# Revit family: ASH_Contour21_Multiproduct_BIM_GB_S6456;S6457;S6458;S6459;S6460;S6461;S6462
name_source: partatom
category: Plumbing Fixtures
revit_build: Autodesk Revit MEP 2014 (Build: 20130308_1515(x64)
units: mm (PartAtom-declared; Revit-internal decimal feet)

## types (35) — shared parameters
AccessibilityPerformance = Doc M
Accessories = www.idealspec.co.uk
AreaUnits = millimeters
Assembly Code = C1030200
AssetType = Fixed
BREEAMApproved = No
Brand = Armitage Shanks
ConnectionType = Plumbing
DurationUnit = year
ECA = No
ExpectedLife = 30
Help = www.idealspec.co.uk/contact-us.html
IfcExportAs = IfcValveType
IfcExportType = FAUCET
InstallationInstructions = www.idealspec.co.uk/resources.html
LinearUnits = millimeters
ManufacturerURL = www.idealspec.co.uk
Material = Brass
NBSDescription = Support rails
NBSReference = 45-35-70/360
NettWeight = 0.62 Kg
NominalHeight = 35 mm  [stored 0.114829 ft]
NominalWidth = 100 mm  [stored 0.328084 ft]
Shape = Sculptured
Space = Internal
SpareParts = www.fastpart-spares.co.uk
TMV3 = Yes
URL = www.idealspec.co.uk
Uniclass2015Description = Support Rails
Uniclass2015Reference = Pr_40_20_76_84
Uniclass2015Version = Products v1.1
Version = 1
VolumeUnits = Litres
WRAS = Yes
WarrantyDescription = Manufacturers Warranty
WarrantyDurationParts = 5
WarrantyDurationUnit = year
WaterEfficientProduct = No
zero-valued in all types: CWFU, Cost, Default Elevation, HWFU, WFU

## per-type parameters (varying)
| type | BIMObjectName | BarCode | Color | Description | Features | Finish | FinishMtl | Model | ModelNumber | ModelReference | Name | NominalLength | ProductInformation | Size |
| S645736 - Contour21 800 x 350mm - Blue | ASH_ArmitageShanks_GrabRails_Contour21_S645736 | 5017830384915 | Blue | Contour21 800 x 350mm, blue | 800 x 350mm, blue | Blue | ASH_ArmitageShanks_Brassware_Blue_36_Render | S645736 | S645736 | Contour21 800 x 350mm, blue | GrabRails_Contour21_S645736_ArmitageShanks | 800 mm  [stored 2.62467 ft] | www.idealspec.co.uk/assets/datasheet/S645736 | 35 x 800 x 100 mm |
| S645839 - Contour21 900 x 350mm - Blue | ASH_ArmitageShanks_GrabRails_Contour21_S645839 | 0 | Blue | Contour21 900 x 350mm, blue | 900 x 350mm, blue | Blue | ASH_ArmitageShanks_Brassware_Blue_36_Render | S645839 | S645839 | Contour21 900 x 350mm, blue | GrabRails_Contour21_S645839_ArmitageShanks | 900 mm  [stored 2.95276 ft] | www.idealspec.co.uk/assets/datasheet/S645839 | 35 x 900 x 100 mm |
| S645936 - Contour21 1000 x 350mm - Blue | ASH_ArmitageShanks_GrabRails_Contour21_S645936 | 5017830384939 | Blue | Contour21 1000 x 350mm, blue | 1000 x 350mm, blue | Blue | ASH_ArmitageShanks_Brassware_Blue_36_Render | S645936 | S645936 | Contour21 1000 x 350mm, blue | GrabRails_Contour21_S645936_ArmitageShanks | 1000 mm  [stored 3.28084 ft] | www.idealspec.co.uk/assets/datasheet/S645936 | 35 x 1000 x 100 mm |
| S646036 - Contour21 1100 x 350mm - Blue | ASH_ArmitageShanks_GrabRails_Contour21_S646036 | 5017830384946 | Blue | Contour21 1100 x 350mm, blue | 1100 x 350mm, blue | Blue | ASH_ArmitageShanks_Brassware_Blue_36_Render | S646036 | S646036 | Contour21 1100 x 350mm, blue | GrabRails_Contour21_S646036_ArmitageShanks | 1100 mm | www.idealspec.co.uk/assets/datasheet/S646036 | 35 x 1100 x 100 mm |
| S646136 - Contour21 1200 x 350mm - Blue | ASH_ArmitageShanks_GrabRails_Contour21_S646136 | 5017830384953 | Blue | Contour21 1200 x 350mm, blue | 1200 x 350mm, blue | Blue | ASH_ArmitageShanks_Brassware_Blue_36_Render | S646136 | S646136 | Contour21 1200 x 350mm, blue | GrabRails_Contour21_S646136_ArmitageShanks | 1200 mm | www.idealspec.co.uk/assets/datasheet/S646136 | 35 x 1200 x 100 mm |
| S646236 - Contour21 1750 x 350mm - Blue | ASH_ArmitageShanks_GrabRails_Contour21_S646236 | 5017830384960 | Blue | Contour21 1750 x 350mm, blue | 1750 x 350mm, blue | Blue | ASH_ArmitageShanks_Brassware_Blue_36_Render | S646236 | S646236 | Contour21 1750 x 350mm, blue | GrabRails_Contour21_S646236_ArmitageShanks | 1750 mm  [stored 5.74147 ft] | www.idealspec.co.uk/assets/datasheet/S646236 | 35 x 1750 x 100 mm |
| S6457AC - Contour21 800 x 350mm - White | ASH_ArmitageShanks_GrabRails_Contour21_S6457AC | 5017830383796 | White | Contour21 800 x 350mm, white | 800 x 350mm, white | White | ASH_ArmitageShanks_Brassware_White_AC_Render | S6457AC | S6457AC | Contour21 800 x 350mm, white | GrabRails_Contour21_S6457AC_ArmitageShanks | 800 mm  [stored 2.62467 ft] | www.idealspec.co.uk/assets/datasheet/S6457AC | 35 x 800 x 100 mm |
| S6457LJ - Contour21 800 x 350mm - Grey | ASH_ArmitageShanks_GrabRails_Contour21_S6457LJ | 5017830384595 | Grey | Contour21 800 x 350mm, grey | 800 x 350mm, grey | Grey | ASH_ArmitageShanks_Brassware_Grey_LJ_Render | S6457LJ | S6457LJ | Contour21 800 x 350mm, grey | GrabRails_Contour21_S6457LJ_ArmitageShanks | 800 mm  [stored 2.62467 ft] | www.idealspec.co.uk/assets/datasheet/S6457LJ | 35 x 800 x 100 mm |
| S6457MY - Contour21 800 x 350mm - Stainless Steel | ASH_ArmitageShanks_GrabRails_Contour21_S6457MY | 5017830384274 | Steel | Contour21 800 x 350mm, stainless steel | 800 x 350mm, stainless steel | Steel | ASH_ArmitageShanks_Brassware_Steel_MY_Render | S6457MY | S6457MY | Contour21 800 x 350mm, stainless steel | GrabRails_Contour21_S6457MY_ArmitageShanks | 800 mm  [stored 2.62467 ft] | www.idealspec.co.uk/assets/datasheet/S6457MY | 35 x 800 x 100 mm |
| S6457RN - Contour21 800 x 350mm - Charcoal | ASH_ArmitageShanks_GrabRails_Contour21_S6457RN | 0 | Charcoal | Contour21 800 x 350mm, charcoal | 800 x 350mm, charcoal | Charcoal | ASH_ArmitageShanks_Brassware_Charcoal_RN_Render | S6457RN | S6457RN | Contour21 800 x 350mm, charcoal | GrabRails_Contour21_S6457RN_ArmitageShanks | 800 mm  [stored 2.62467 ft] | www.idealspec.co.uk/assets/datasheet/S6457RN | 35 x 800 x 100 mm |
| S6459AC - Contour21 1000 x 350mm - White | ASH_ArmitageShanks_GrabRails_Contour21_S6459AC | 5017830383819 | White | Contour21 1000 x 350mm, white | 1000 x 350mm, white | White | ASH_ArmitageShanks_Brassware_White_AC_Render | S6459AC | S6459AC | Contour21 1000 x 350mm, white | GrabRails_Contour21_S6459AC_ArmitageShanks | 1000 mm  [stored 3.28084 ft] | www.idealspec.co.uk/assets/datasheet/S6459AC | 35 x 1000 x 100 mm |
| S6459LJ - Contour21 1000 x 350mm - Grey | ASH_ArmitageShanks_GrabRails_Contour21_S6459LJ | 5017830384618 | Grey | Contour21 1000 x 350mm, grey | 1000 x 350mm, grey | Grey | ASH_ArmitageShanks_Brassware_Grey_LJ_Render | S6459LJ | S6459LJ | Contour21 1000 x 350mm, grey | GrabRails_Contour21_S6459LJ_ArmitageShanks | 1000 mm  [stored 3.28084 ft] | www.idealspec.co.uk/assets/datasheet/S6459LJ | 35 x 1000 x 100 mm |
| S6459MY - Contour21 1000 x 350mm - Stainless Steel | ASH_ArmitageShanks_GrabRails_Contour21_S6459MY | 5017830384298 | Steel | Contour21 1000 x 350mm, stainless steel | 1000 x 350mm, stainless steel | Steel | ASH_ArmitageShanks_Brassware_Steel_MY_Render | S6459MY | S6459MY | Contour21 1000 x 350mm, stainless steel | GrabRails_Contour21_S6459MY_ArmitageShanks | 1000 mm  [stored 3.28084 ft] | www.idealspec.co.uk/assets/datasheet/S6459MY | 35 x 1000 x 100 mm |
| S6459RN - Contour21 1000 x 350mm - Charcoal | ASH_ArmitageShanks_GrabRails_Contour21_S6459RN | 5017830388470 | Charcoal | Contour21 1000 x 350mm, charcoal | 1000 x 350mm, charcoal | Charcoal | ASH_ArmitageShanks_Brassware_Charcoal_RN_Render | S6459RN | S6459RN | Contour21 1000 x 350mm, charcoal | GrabRails_Contour21_S6459RN_ArmitageShanks | 1000 mm  [stored 3.28084 ft] | www.idealspec.co.uk/assets/datasheet/S6459RN | 35 x 1000 x 100 mm |
| S6460AC - Contour21 1100 x 350mm - White | ASH_ArmitageShanks_GrabRails_Contour21_S6460AC | 5017830383826 | White | Contour21 1100 x 350mm, white | 1100 x 350mm, white | White | ASH_ArmitageShanks_Brassware_White_AC_Render | S6460AC | S6460AC | Contour21 1100 x 350mm, white | GrabRails_Contour21_S6460AC_ArmitageShanks | 1100 mm | www.idealspec.co.uk/assets/datasheet/S6460AC | 35 x 1100 x 100 mm |
| S6460LJ - Contour21 1100 x 350mm - Grey | ASH_ArmitageShanks_GrabRails_Contour21_S6460LJ | 5017830384625 | Grey | Contour21 1100 x 350mm, grey | 1100 x 350mm, grey | Grey | ASH_ArmitageShanks_Brassware_Grey_LJ_Render | S6460LJ | S6460LJ | Contour21 1100 x 350mm, grey | GrabRails_Contour21_S6460LJ_ArmitageShanks | 1100 mm | www.idealspec.co.uk/assets/datasheet/S6460LJ | 35 x 1100 x 100 mm |
| S6460MY - Contour21 1100 x 350mm - Stainless Steel | ASH_ArmitageShanks_GrabRails_Contour21_S6460MY | 5017830384304 | Steel | Contour21 1100 x 350mm, stainless steel | 1100 x 350mm, stainless steel | Steel | ASH_ArmitageShanks_Brassware_Steel_MY_Render | S6460MY | S6460MY | Contour21 1100 x 350mm, stainless steel | GrabRails_Contour21_S6460MY_ArmitageShanks | 1100 mm | www.idealspec.co.uk/assets/datasheet/S6460MY | 35 x 1100 x 100 mm |
| S6460RN - Contour21 1100 x 350mm - Charcoal | ASH_ArmitageShanks_GrabRails_Contour21_S6460RN | 5017830388487 | Charcoal | Contour21 1100 x 350mm, charcoal | 1100 x 350mm, charcoal | Charcoal | ASH_ArmitageShanks_Brassware_Charcoal_RN_Render | S6460RN | S6460RN | Contour21 1100 x 350mm, charcoal | GrabRails_Contour21_S6460RN_ArmitageShanks | 1100 mm | www.idealspec.co.uk/assets/datasheet/S6460RN | 35 x 1100 x 100 mm |
| S6461AC - Contour21 1200 x 350mm - White | ASH_ArmitageShanks_GrabRails_Contour21_S6461AC | 5017830383833 | White | Contour21 1200 x 350mm, white | 1200 x 350mm, white | White | ASH_ArmitageShanks_Brassware_White_AC_Render | S6461AC | S6461AC | Contour21 1200 x 350mm, white | GrabRails_Contour21_S6461AC_ArmitageShanks | 1200 mm | www.idealspec.co.uk/assets/datasheet/S6461AC | 35 x 1200 x 100 mm |
| S6461LJ - Contour21 1200 x 350mm - Grey | ASH_ArmitageShanks_GrabRails_Contour21_S6461LJ | 5017830384632 | Grey | Contour21 1200 x 350mm, grey | 1200 x 350mm, grey | Grey | ASH_ArmitageShanks_Brassware_Grey_LJ_Render | S6461LJ | S6461LJ | Contour21 1200 x 350mm, grey | GrabRails_Contour21_S6461LJ_ArmitageShanks | 1200 mm | www.idealspec.co.uk/assets/datasheet/S6461LJ | 35 x 1200 x 100 mm |
| S6461MY - Contour21 1200 x 350mm - Stainless Steel | ASH_ArmitageShanks_GrabRails_Contour21_S6461MY | 5017830384311 | Steel | Contour21 1200 x 350mm, stainless steel | 1200 x 350mm, stainless steel | Steel | ASH_ArmitageShanks_Brassware_Steel_MY_Render | S6461MY | S6461MY | Contour21 1200 x 350mm, stainless steel | GrabRails_Contour21_S6461MY_ArmitageShanks | 1200 mm | www.idealspec.co.uk/assets/datasheet/S6461MY | 35 x 1200 x 100 mm |
| S6461RN - Contour21 1200 x 350mm - Charcoal | ASH_ArmitageShanks_GrabRails_Contour21_S6461RN | 5017830388494 | Charcoal | Contour21 1200 x 350mm, charcoal | 1200 x 350mm, charcoal | Charcoal | ASH_ArmitageShanks_Brassware_Charcoal_RN_Render | S6461RN | S6461RN | Contour21 1200 x 350mm, charcoal | GrabRails_Contour21_S6461RN_ArmitageShanks | 1200 mm | www.idealspec.co.uk/assets/datasheet/S6461RN | 35 x 1200 x 100 mm |
| S6458AC - Contour21 900 x 350mm - White | ASH_ArmitageShanks_GrabRails_Contour21_S6458AC | 5017830383802 | White | Contour21 900 x 350mm, white | 900 x 350mm, white | White | ASH_ArmitageShanks_Brassware_White_AC_Render | S6458AC | S6458AC | Contour21 900 x 350mm, white | GrabRails_Contour21_S6458AC_ArmitageShanks | 900 mm  [stored 2.95276 ft] | www.idealspec.co.uk/assets/datasheet/S6458AC | 35 x 900 x 100 mm |
| S6458LJ - Contour21 900 x 350mm - Grey | ASH_ArmitageShanks_GrabRails_Contour21_S6458LJ | 5017830384601 | Grey | Contour21 900 x 350mm, grey | 900 x 350mm, grey | Grey | ASH_ArmitageShanks_Brassware_Grey_LJ_Render | S6458LJ | S6458LJ | Contour21 900 x 350mm, grey | GrabRails_Contour21_S6458LJ_ArmitageShanks | 900 mm  [stored 2.95276 ft] | www.idealspec.co.uk/assets/datasheet/S6458LJ | 35 x 900 x 100 mm |
| S6458MY - Contour21 900 x 350mm - Stainless Steel | ASH_ArmitageShanks_GrabRails_Contour21_S6458MY | 5017830384281 | Steel | Contour21 900 x 350mm, stainless steel | 900 x 350mm, stainless steel | Steel | ASH_ArmitageShanks_Brassware_Steel_MY_Render | S6458MY | S6458MY | Contour21 900 x 350mm, stainless steel | GrabRails_Contour21_S6458MY_ArmitageShanks | 900 mm  [stored 2.95276 ft] | www.idealspec.co.uk/assets/datasheet/S6458MY | 35 x 900 x 100 mm |
| S6458RN - Contour21 900 x 350mm - Charcoal | ASH_ArmitageShanks_GrabRails_Contour21_S6458RN | 5017830388463 | Charcoal | Contour21 900 x 350mm, charcoal | 900 x 350mm, charcoal | Charcoal | ASH_ArmitageShanks_Brassware_Charcoal_RN_Render | S6458RN | S6458RN | Contour21 900 x 350mm, charcoal | GrabRails_Contour21_S6458RN_ArmitageShanks | 900 mm  [stored 2.95276 ft] | www.idealspec.co.uk/assets/datasheet/S6458RN | 35 x 900 x 100 mm |
| S6462AC - Contour21 1750 x 350mm - White | ASH_ArmitageShanks_GrabRails_Contour21_S6462AC | 5017830383840 | White | Contour21 1750 x 350mm, white | 1750 x 350mm, white | White | ASH_ArmitageShanks_Brassware_White_AC_Render | S6462AC | S6462AC | Contour21 1750 x 350mm, white | GrabRails_Contour21_S6462AC_ArmitageShanks | 1750 mm  [stored 5.74147 ft] | www.idealspec.co.uk/assets/datasheet/S6462AC | 35 x 1750 x 100 mm |
| S6462LJ - Contour21 1750 x 350mm - Grey | ASH_ArmitageShanks_GrabRails_Contour21_S6462LJ | 5017830384649 | Grey | Contour21 1750 x 350mm, grey | 1750 x 350mm, grey | Grey | ASH_ArmitageShanks_Brassware_Grey_LJ_Render | S6462LJ | S6462LJ | Contour21 1750 x 350mm, grey | GrabRails_Contour21_S6462LJ_ArmitageShanks | 1750 mm  [stored 5.74147 ft] | www.idealspec.co.uk/assets/datasheet/S6462LJ | 35 x 1750 x 100 mm |
| S6462MY - Contour21 1750 x 350mm - Stainless Steel | ASH_ArmitageShanks_GrabRails_Contour21_S6462MY | 5017830384328 | Steel | Contour21 1750 x 350mm, stainless steel | 1750 x 350mm, stainless steel | Steel | ASH_ArmitageShanks_Brassware_Steel_MY_Render | S6462MY | S6462MY | Contour21 1750 x 350mm, stainless steel | GrabRails_Contour21_S6462MY_ArmitageShanks | 1750 mm  [stored 5.74147 ft] | www.idealspec.co.uk/assets/datasheet/S6462MY | 35 x 1750 x 100 mm |
| S6462RN - Contour21 1750 x 350mm - Charcoal | ASH_ArmitageShanks_GrabRails_Contour21_S6462RN | 5017830388500 | Charcoal | Contour21 1750 x 350mm, charcoal | 1750 x 350mm, charcoal | Charcoal | ASH_ArmitageShanks_Brassware_Charcoal_RN_Render | S6462RN | S6462RN | Contour21 1750 x 350mm, charcoal | GrabRails_Contour21_S6462RN_ArmitageShanks | 1750 mm  [stored 5.74147 ft] | www.idealspec.co.uk/assets/datasheet/S6462RN | 35 x 1750 x 100 mm |
| S645636 - Contour21 750 x 350mm - Blue | ASH_ArmitageShanks_GrabRails_Contour21_S645636 | 5017830384908 | Blue | Contour21 750 x 350mm, blue | 750 x 350mm, blue | Blue | ASH_ArmitageShanks_Brassware_Blue_36_Render | S645636 | S645636 | Contour21 750 x 350mm, blue | GrabRails_Contour21_S645636_ArmitageShanks | 750 mm  [stored 2.46063 ft] | www.idealspec.co.uk/assets/datasheet/S645636 | 35 x 750 x 100 mm |
| S6456AC - Contour21 750 x 350mm - White | ASH_ArmitageShanks_GrabRails_Contour21_S6456AC | 5017830384175 | White | Contour21 750 x 350mm, white | 750 x 350mm, white | White | ASH_ArmitageShanks_Brassware_White_AC_Render | S6456AC | S6456AC | Contour21 750 x 350mm, white | GrabRails_Contour21_S6456AC_ArmitageShanks | 750 mm  [stored 2.46063 ft] | www.idealspec.co.uk/assets/datasheet/S6456AC | 35 x 750 x 100 mm |
| S6456LJ - Contour21 750 x 350mm - Grey | ASH_ArmitageShanks_GrabRails_Contour21_S6456LJ | 5017830384588 | Grey | Contour21 750 x 350mm, grey | 750 x 350mm, grey | Grey | ASH_ArmitageShanks_Brassware_Grey_LJ_Render | S6456LJ | S6456LJ | Contour21 750 x 350mm, grey | GrabRails_Contour21_S6456LJ_ArmitageShanks | 750 mm  [stored 2.46063 ft] | www.idealspec.co.uk/assets/datasheet/S6456LJ | 35 x 750 x 100 mm |
| S6456MY - Contour21 750 x 350mm - Stainless Steel | ASH_ArmitageShanks_GrabRails_Contour21_S6456MY | 5017830384267 | Steel | Contour21 750 x 350mm, stainless steel | 750 x 350mm, stainless steel | Steel | ASH_ArmitageShanks_Brassware_Steel_MY_Render | S6456MY | S6456MY | Contour21 750 x 350mm, stainless steel | GrabRails_Contour21_S6456MY_ArmitageShanks | 750 mm  [stored 2.46063 ft] | www.idealspec.co.uk/assets/datasheet/S6456MY | 35 x 750 x 100 mm |
| S6456RN - Contour21 750 x 350mm - Charcoal | ASH_ArmitageShanks_GrabRails_Contour21_S6456RN | 5017830388449 | Charcoal | Contour21 750 x 350mm, charcoal | 750 x 350mm, charcoal | Charcoal | ASH_ArmitageShanks_Brassware_Charcoal_RN_Render | S6456RN | S6456RN | Contour21 750 x 350mm, charcoal | GrabRails_Contour21_S6456RN_ArmitageShanks | 750 mm  [stored 2.46063 ft] | www.idealspec.co.uk/assets/datasheet/S6456RN | 35 x 750 x 100 mm |

note: [stored X ft] marks values corroborated as IEEE doubles in the binary element streams (Revit-internal decimal feet)

## geometry (parser evidence)
native form markers: Sweep x2
no freeform markers — native parametric forms only
